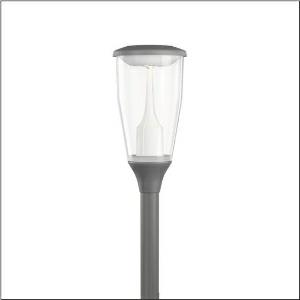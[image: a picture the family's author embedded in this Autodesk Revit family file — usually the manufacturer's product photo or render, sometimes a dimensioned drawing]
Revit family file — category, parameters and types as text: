
# Revit family: dl_11_iq___st1_2a_5xa5575mf14h000022_93a8
name_source: partatom
category: Lighting Fixtures
units: mm (PartAtom-declared; Revit-internal decimal feet)

## family parameters
Cut with Voids When Loaded = No
Host = Face
Light Source = No
Part Type = Normal
Room Calculation Point = No
Round Connector Dimension = Use Diameter
Shared = No

## types (1)
- --- (1 x LED, 1560 lm, 11.8 W, 2700K)
    Apparent Load = 12 VA
    CIE Flux Codes = 24 63 94 96 100
    Color Rendering = 70
    Color Temperature = 2700K
    Default Elevation = 1800 mm
    Description = DL 11 iQ, mast luminaire, Module 540 iQ-SR, primary light control with 3 zone facetted reflector, of plastic, silver coated, highly specular, structured, primary optical cover: cover, of PMMA, transparent, light distribution: ST1.2a, light emission: direct distribution, primary light characteristic: asymmetric, installation type: post-top, LED, High Power LED, rated luminous flux: 1.560lm, luminous efficacy: 149lm/W, light colour: 727, colour temperature: 2700K, control gear: iQ Street-Remote, control: Street-Remote, Auto-Match, Temp-Guard, Lumen-Switch, Night-Set, Smart-Wire, Light-Fading, Desk-Remote (wireless, voltage-free reading and setting of iQ features in the workshop via application-optimized NFC function/RFID function), optimised constant luminous flux control (CLO 2.0), mains connection: 220..240V, AC, 50/60Hz, connection cable pre-assembled, cable length: 5,5m, wiring characteristics: H07RN-F, 5-core, 1.5mm², start of lifetime: 12W, end of service life: 12W, reduction: 5W, luminaire housing, upper part, of diecast aluminium, coated, Siteco® metallic grey (DB 702S), spigot size: 76mm (post-top), mounting height: 3..5m, post-top mast mounting element, of diecast aluminium, coated, Siteco® metallic grey (DB 702S), Module 540 iQ-SR, traffic white (RAL 9016), equipment: standard, protection rating (complete): IP66, insulation class (complete): insulation class II (safety insulation), certification: CE, ENEC, ENEC+, VDE, impact resistance: IK07, packaging unit: 1 piece

Light Distribution: ST1.2a
    Height = 665 mm
    Lamp = 1 x LED
    Lamp Light Flux = 1560 lm
    Lamp Power = 11.8 W
    Lamp count = 1
    Length = 334 mm
    Luminous efficacy = 132 lm/W
    Manufacturer = Siteco
    ModVariant = No
    Model = 5XA5575MF14H000022
    Number of Poles = 1
    OnlyDefault = Yes
    Power Factor = 1
    Product Name = DL 11 iQ | ST1.2a
    Product group = mast luminaire | pylon top
    ProductGroupID = 6100
    Protection Class = Protection class II
    Protection Degree = IP 66
    RLX_Detail_Level = 1
    RLX_Emergency_Light_Flux = 0 lm
    RLX_Emergency_Type = 0
    RLX_Emergency_Type_DB = No
    RlxData = <blob elided: 139545 chars, md5=3b96fb72>
    Socket = socket
    Standby Power = 0 W
    System Light Flux = 1560 lm
    System Power = 12 W
    Type Comments = factory setting: luminous flux: 100 % | dim-lin: 254 | 472 mA
    Type Image = l_1258354.jpg
    URL = http://relux.com
    VarID = @adj_116425
    Voltage = 0 V
    Weight = 0.00 kg
    Width = 0 mm  [stored 0 ft]

note: [stored X ft] marks values corroborated as IEEE doubles in the binary element streams (Revit-internal decimal feet)

## geometry (parser evidence)
native form markers: Blend x4, Sweep x10
no freeform markers — native parametric forms only
